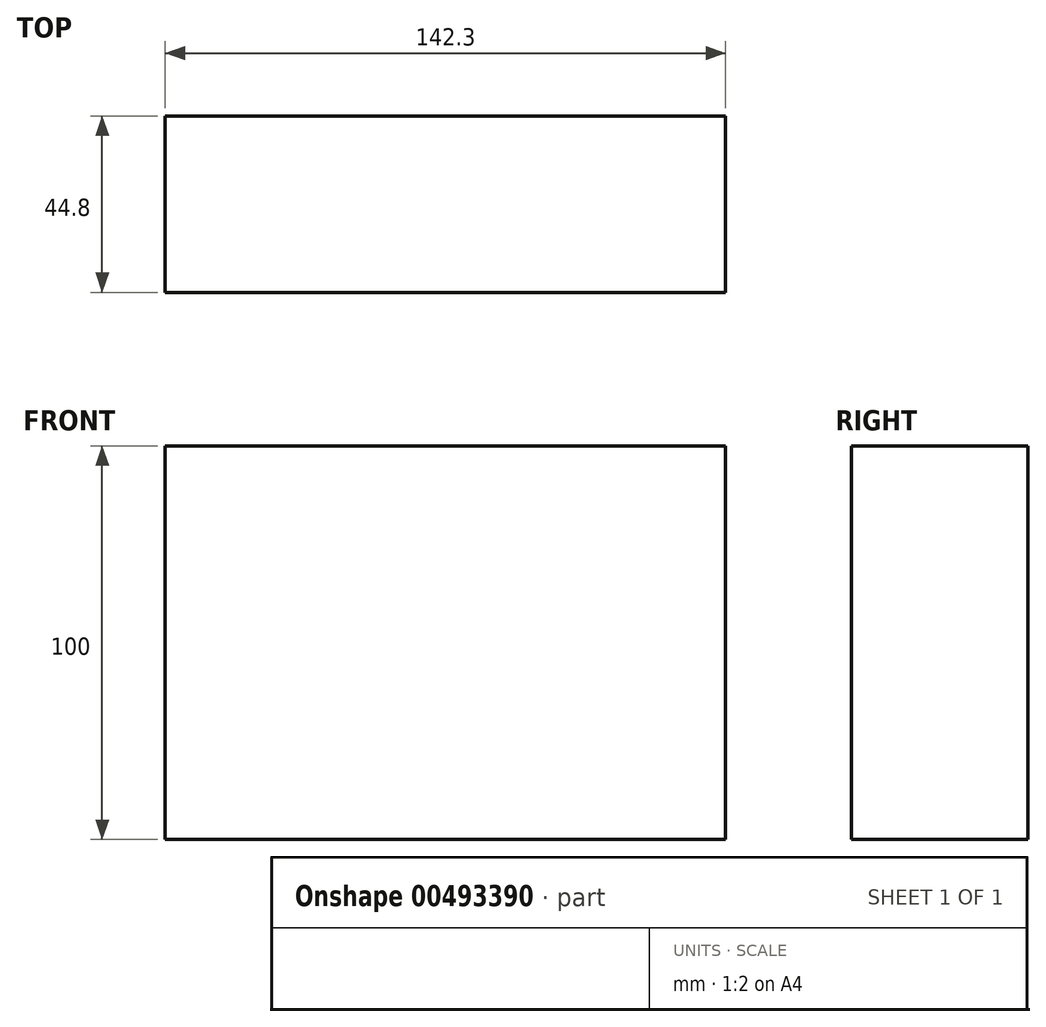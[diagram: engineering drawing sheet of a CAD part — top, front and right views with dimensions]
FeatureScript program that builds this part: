
annotation { "Feature Type Name" : "Feature", "Feature Type Description" : "" }
export const myFeature = defineFeature(function(context is Context, id is Id, definition is map)
    precondition{}
    {
        {
            var Q0;
            Q0=qCreatedBy(makeId("Top.planeOp"),FACE);
            var sketch = newSketch(context, id + "F0", { "sketchPlane" : qUnion([Q0])});
            skLineSegment(sketch, "E0.bottom", {"start": v(-71.15, -22.4) * mm, "end": v(71.15, -22.4) * mm});
            skLineSegment(sketch, "E0.top", {"start": v(-71.15, 22.4) * mm, "end": v(71.15, 22.4) * mm});
            skLineSegment(sketch, "E0.left", {"start": v(-71.15, -22.4) * mm, "end": v(-71.15, 22.4) * mm});
            skLineSegment(sketch, "E0.right", {"start": v(71.15, -22.4) * mm, "end": v(71.15, 22.4) * mm});
            skPoint(sketch, "E0.middle", {"position": v(0, 0) * mm});
            skSolve(sketch);
        }
        {
            var Q0;
            Q0=makeQuery(id+"F0.imprint","IMPRINT",FACE,{"disambiguationData":[TD([[makeQuery(id+"F0.imprint","IMPRINT",EDGE,{"derivedFrom":sQuery(id+"F0.wireOp",EDGE,"E0.bottom")}),1.0]])]});
            extrude(context, id + "F1", {"entities" : qUnion([Q0]), "endBound" : BoundingType.SYMMETRIC, "depth" : 100 * mm});
        }
    });
